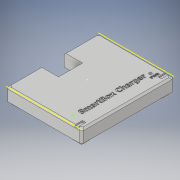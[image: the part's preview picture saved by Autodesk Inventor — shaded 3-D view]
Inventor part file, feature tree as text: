
AUTODESK INVENTOR PART (.ipt)
format: ipt  version: 2019 (Build 230136000, 136)  size: 1,077,248 bytes
history: native  units: mm
features: sketch x25, extrude x20, move_body x18, direct_edit x11, draft x2, chamfer x2
ambient origin geometry x8: Origin, YZ Plane, XZ Plane, XY Plane, X Axis, Y Axis, Z Axis, Center Point
bodies: Solid1 (feature_tree)
feature tree (78):
  extrude  "Extrusion1"  Depth=110.0mm
  extrude  "Extrusion2"  Depth=15.0mm
  sketch  "Sketch3"  dims[d5=21.8mm d6=15.0mm d7=0.0mm]
  direct_edit  "Direct Edit1"
  extrude  "Extrusion3"  Depth=15.0mm TaperAngle=0.0deg
  draft  "FaceDraft1"
  draft  "FaceDraft2"
  sketch  "Sketch5"  dims[d12=15.0mm d13=7.0mm]
  extrude  "Extrusion4"  Depth=7.0mm
  extrude  "Extrusion5"  Depth=15.0mm
  extrude  "Extrusion6"  Depth=15.0mm TaperAngle=0.0deg
  extrude  "Extrusion7"  Depth=1.745329mm
  extrude  "Extrusion8"  Depth=12.0mm TaperAngle=0.0deg
  direct_edit  "Direct Edit2"
  direct_edit  "Direct Edit3"
  sketch  "Sketch11"  dims[d29=5.0mm d30=5.0mm]
  extrude  "Extrusion9"  Depth=31.5mm
  sketch  "Sketch13"  dims[d33=5.0mm d34=10.0mm]
  extrude  "Extrusion10"  Depth=5.0mm
  sketch  "Sketch14"  dims[d35=10.0mm d36=10.0mm]
  direct_edit  "Direct Edit4"
  extrude  "Extrusion11"  Depth=5.0mm
  direct_edit  "Direct Edit5"
  extrude  "Extrusion12"  Depth=5.0mm
  extrude  "Extrusion13"  Depth=5.0mm
  direct_edit  "Direct Edit6"
  extrude  "Extrusion14"  Depth=10.0mm
  direct_edit  "Direct Edit7"
  direct_edit  "Direct Edit8"
  extrude  "Extrusion15"  Depth=10.0mm
  extrude  "Extrusion16"  Depth=10.0mm
  sketch  "Sketch21"  dims[d51=1.0mm]
  extrude  "Extrusion17"  Depth=15.0mm TaperAngle=0.0deg
  direct_edit  "Direct Edit9"
  extrude  "Extrusion18"  Depth=2.5mm
  direct_edit  "Direct Edit10"
  sketch  "Sketch25"  dims[d59=0.0mm d60=0.0mm d61=-0.3mm]
  extrude  "Extrusion19"  Depth=2.5mm
  direct_edit  "Direct Edit11"
  extrude  "Extrusion20"  Depth=1.0mm
  chamfer  "Chamfer1"  Distance=3.0mm
  chamfer  "Chamfer2"  [1 undecoded]
  sketch  "Sketch1"  dims[d0=84.0mm d1=110.0mm]
  sketch  "Sketch2"  dims[d2=15.0mm d3=0.0mm d4=28.6mm]
  sketch  "Sketch4"  dims[d8=0.0mm d9=0.0mm d10=6.0mm d11=7.0mm]
  sketch  "Sketch6"  dims[d14=15.0mm d15=20.0mm d16=0.0mm]
  sketch  "Sketch7"  dims[d17=1.745329mm d18=1.745329mm]
  sketch  "Sketch8"  dims[d19=2.5mm d20=12.0mm d21=0.0mm]
  sketch  "Sketch9"  dims[d22=4.5mm d23=31.5mm]
  sketch  "Sketch10"  dims[d24=2.2mm d25=0.0mm d28=5.0mm]
  sketch  "Sketch12"  dims[d31=5.0mm d32=5.0mm]
  sketch  "Sketch15"  dims[d37=10.0mm d38=10.0mm]
  sketch  "Sketch16"  dims[d39=10.0mm d40=10.0mm]
  sketch  "Sketch17"  dims[d41=10.0mm d42=15.0mm d43=0.0mm]
  sketch  "Sketch18"  dims[d44=2.5mm d45=2.5mm]
  sketch  "Sketch19"  dims[d46=2.5mm d47=2.5mm]
  sketch  "Sketch20"  dims[d48=3.0mm d49=0.0mm d50=1.0mm]
  sketch  "Sketch22"  dims[d52=1.0mm]
  sketch  "Sketch23"  dims[d53=1.0mm d54=3.0mm d55=0.0mm d56=0.0mm d57=0.0mm d58=-0.3mm]
  sketch  "Sketch26"  dims[d62=0.0mm d63=0.0mm d64=-0.3mm d65=0.0mm d66=0.0mm d67=-0.3mm d68=25.0mm d69=25.0mm d70=25.0mm d71=4.0mm d72=1.0mm d73=9.0mm d74=4.5mm d75=8.5mm d76=3.0mm d77=0.0mm d80=3.2mm d81=4.5mm d82=4.5mm d83=2.0mm d84=0.0mm d85=0.0mm d86=0.0mm d87=-7.75mm d88=10.0mm d89=13.0mm d90=3.0mm d91=0.0mm d92=0.0mm d93=0.0mm d94=6.75mm d95=0.6mm d96=0.0mm d97=0.6mm d98=0.0mm d99=0.0mm d100=0.0mm d101=-2.0mm d102=2.5mm d103=1.0mm d104=0.0mm d105=0.0mm d106=0.0mm d107=0.97mm d108=-4.0mm d109=0.0mm d110=0.0mm d111=0.0mm d112=0.0mm d113=-20.0mm d114=6.0mm d115=15.0mm d116=6.0mm d117=15.0mm d118=20.0mm d119=0.0mm d120=3.5mm d121=20.0mm d122=2.0mm d123=3.5mm d124=20.0mm d125=2.0mm d126=15.0mm d127=0.0mm d128=0.3mm d129=0.3mm d130=0.3mm d131=0.0mm d145=0.0mm d146=0.0mm d147=-0.3mm d148=15.0mm d149=0.0mm d150=0.0mm d151=0.0mm d152=15.0mm d153=0.0mm d154=0.0mm d155=15.0mm d156=0.0mm d157=0.0mm d158=3.5mm d159=0.0mm d160=0.0mm d161=-0.3mm d162=4.0mm d163=0.0mm d164=0.0mm d165=7.5mm d166=7.0mm d167=2.0mm d168=10.0mm d169=2.0mm d170=10.0mm d171=1.5mm d172=0.0mm d173=83.0mm d174=0.0mm d175=0.0mm d176=1.5mm d177=4.0mm d178=10.0mm d179=4.0mm d180=10.0mm d181=1.5mm d182=0.0mm d183=2.0mm d184=2.0mm d185=45.0deg d186=2.0mm d187=2.0mm d188=45.0deg]
  move_body  "Move1"
  move_body  "Move2"
  move_body  "Move3"
  move_body  "Move4"
  move_body  "Move5"
  move_body  "Move6"
  move_body  "Move7"
  move_body  "Move8"
  move_body  "Move9"
  move_body  "Move10"
  move_body  "Move11"
  move_body  "Move12"
  move_body  "Move13"
  move_body  "Move14"
  move_body  "Move15"
  move_body  "Move16"
  move_body  "Move17"
  move_body  "Move18"
note: 1 required parameter value undecoded (feature->parameter linkage not recoverable at this tier; creation-order binding heuristic only, values carry confidence <= 0.55)
